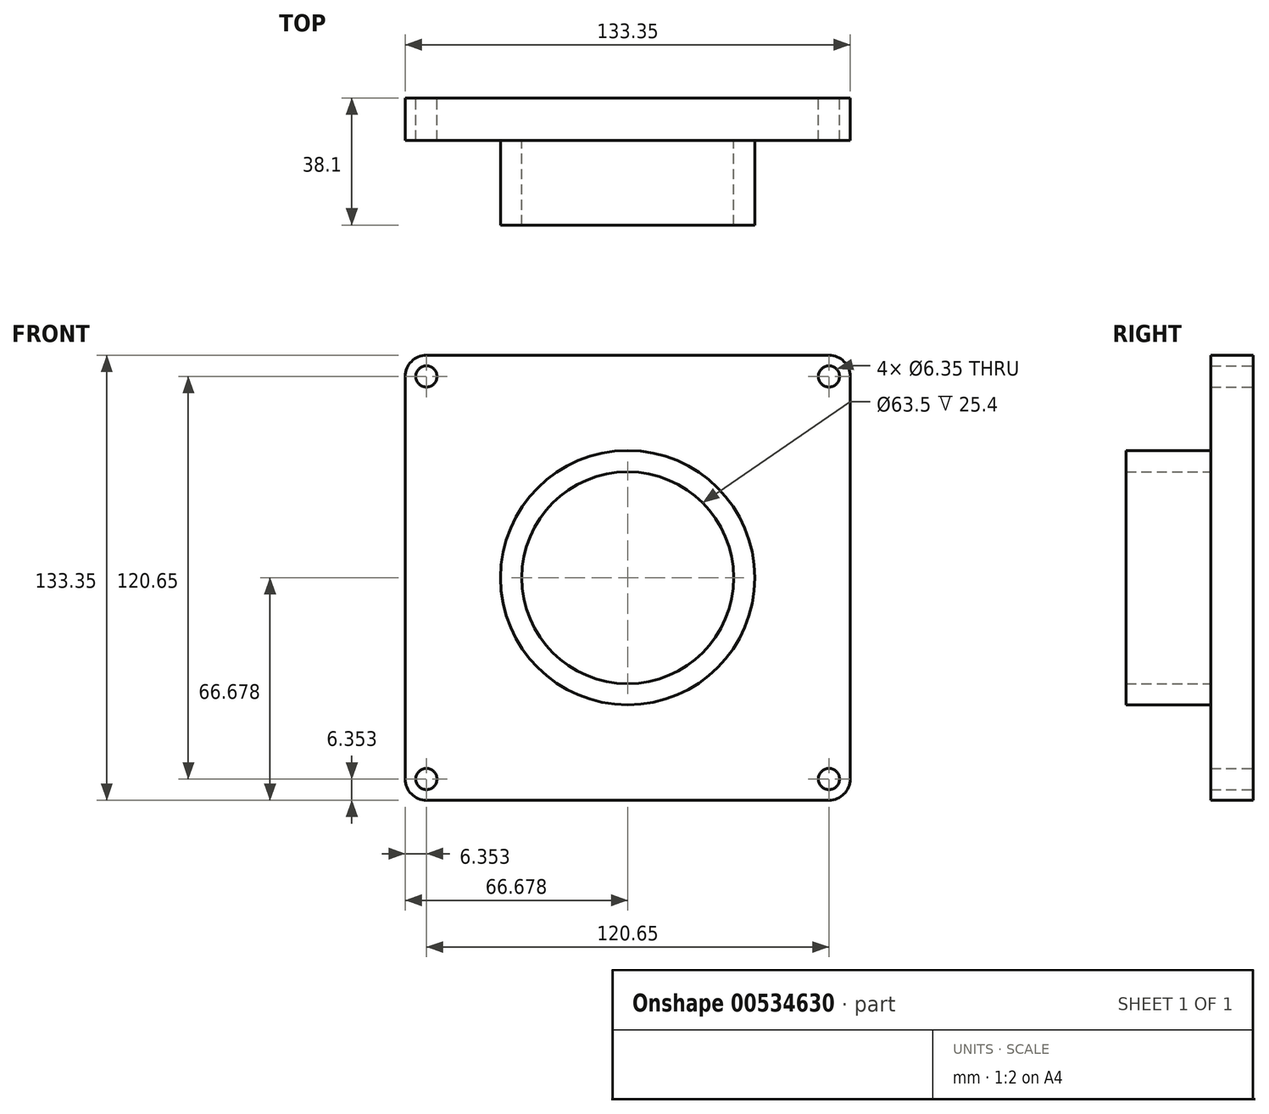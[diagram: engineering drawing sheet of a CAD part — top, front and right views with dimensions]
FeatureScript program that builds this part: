
annotation { "Feature Type Name" : "Feature", "Feature Type Description" : "" }
export const myFeature = defineFeature(function(context is Context, id is Id, definition is map)
    precondition{}
    {
        {
            var Q0;
            Q0=qCreatedBy(makeId("Front.planeOp"),FACE);
            var sketch = newSketch(context, id + "F0", { "sketchPlane" : qUnion([Q0])});
            skLineSegment(sketch, "E0.bottom", {"start": v(-57.45, 85.67) * mm, "end": v(63.2, 85.67) * mm});
            skLineSegment(sketch, "E0.top", {"start": v(-57.45, -47.68) * mm, "end": v(63.2, -47.68) * mm});
            skLineSegment(sketch, "E0.left", {"start": v(-63.8, 79.32) * mm, "end": v(-63.8, -41.33) * mm});
            skLineSegment(sketch, "E0.right", {"start": v(69.55, 79.32) * mm, "end": v(69.55, -41.33) * mm});
            skCircle(sketch, "E1", {"center": v(-57.45, 79.32) * mm, "radius": 3.18 * mm});
            skCircle(sketch, "E2", {"center": v(-57.45, -41.33) * mm, "radius": 3.18 * mm});
            skCircle(sketch, "E3", {"center": v(63.2, 79.32) * mm, "radius": 3.18 * mm});
            skCircle(sketch, "E4", {"center": v(63.2, -41.33) * mm, "radius": 3.18 * mm});
            skPoint(sketch, "E5.visualSharp", {"position": v(-63.8, 85.67) * mm});
            skArc(sketch, "E5.filletArc", {"start": v(-57.45, 85.67) * mm, "mid": v(-61.94, 83.81) * mm, "end": v(-63.8, 79.32) * mm});
            skPoint(sketch, "E6.visualSharp", {"position": v(-63.8, -47.68) * mm});
            skArc(sketch, "E6.filletArc", {"start": v(-63.8, -41.33) * mm, "mid": v(-61.94, -45.82) * mm, "end": v(-57.45, -47.68) * mm});
            skPoint(sketch, "E7.visualSharp", {"position": v(69.55, -47.68) * mm});
            skArc(sketch, "E7.filletArc", {"start": v(63.2, -47.68) * mm, "mid": v(67.7, -45.82) * mm, "end": v(69.55, -41.33) * mm});
            skPoint(sketch, "E8.visualSharp", {"position": v(69.55, 85.67) * mm});
            skArc(sketch, "E8.filletArc", {"start": v(69.55, 79.32) * mm, "mid": v(67.7, 83.81) * mm, "end": v(63.2, 85.67) * mm});
            skSolve(sketch);
        }
        {
            var Q0;
            Q0=makeQuery(id+"F0.imprint","IMPRINT",FACE,{"disambiguationData":[TD([[makeQuery(id+"F0.imprint","IMPRINT",EDGE,{"derivedFrom":sQuery(id+"F0.wireOp",EDGE,"E0.bottom")}),-1.0]])]});
            extrude(context, id + "F1", {"entities" : qUnion([Q0]), "depth" : 12.7 * mm, "offsetDistance" : 25.4 * mm});
        }
        {
            var Q0;
            Q0=makeQuery(id+"F1.opExtrude","CAP_FACE",FACE,{"disambiguationData":[OSD([sQuery(id+"F0.wireOp",EDGE,"E0.bottom"),sQuery(id+"F0.wireOp",EDGE,"E0.top"),sQuery(id+"F0.wireOp",EDGE,"E0.left"),sQuery(id+"F0.wireOp",EDGE,"E0.right"),sQuery(id+"F0.wireOp",EDGE,"E1"),sQuery(id+"F0.wireOp",EDGE,"E2"),sQuery(id+"F0.wireOp",EDGE,"E3"),sQuery(id+"F0.wireOp",EDGE,"E4"),sQuery(id+"F0.wireOp",EDGE,"E5.filletArc"),sQuery(id+"F0.wireOp",EDGE,"E6.filletArc"),sQuery(id+"F0.wireOp",EDGE,"E7.filletArc"),sQuery(id+"F0.wireOp",EDGE,"E8.filletArc")])],"isStart":false});
            var sketch = newSketch(context, id + "F2", { "sketchPlane" : qUnion([Q0])});
            skCircle(sketch, "E9", {"center": v(2.88, 19) * mm, "radius": 31.75 * mm});
            skPoint(sketch, "E9.centerSnap0", {"position": v(2.88, 85.67) * mm});
            skPoint(sketch, "E9.centerSnap1", {"position": v(-63.8, 19) * mm});
            skCircle(sketch, "E10.0", {"center": v(2.88, 19) * mm, "radius": 38.1 * mm});
            skSolve(sketch);
        }
        {
            var Q0;
            Q0=makeQuery(id+"F2.imprint","IMPRINT",FACE,{"disambiguationData":[TD([[makeQuery(id+"F2.imprint","IMPRINT",EDGE,{"derivedFrom":sQuery(id+"F2.wireOp",EDGE,"E9")}),-1.0]])]});
            extrude(context, id + "F3", {"entities" : qUnion([Q0]), "operationType" : NewBodyOperationType.ADD, "depth" : 25.4 * mm, "offsetDistance" : 25.4 * mm});
        }
    });
